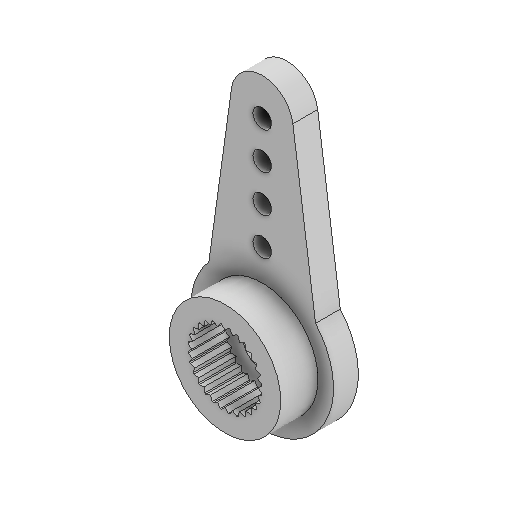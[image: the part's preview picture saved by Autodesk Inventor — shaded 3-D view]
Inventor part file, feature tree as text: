
AUTODESK INVENTOR PART (.ipt)
format: ipt  version: 2025.1 (Build 291241000, 241)  size: 228,352 bytes
history: native  units: mm
features: other x2, extrude x1, sketch x1
ambient origin geometry x8: Origin, YZ Plane, XZ Plane, XY Plane, X Axis, Y Axis, Z Axis, Center Point
bodies: Body1 (feature_tree)
feature tree (4):
  other  "Bryła1"
  extrude  "Wyciągnięcie proste1"  Depth=10.0mm TaperAngle=0.0deg
  sketch  "Szkic1"
  other  "Enlèv. mat.-Extru.5"
